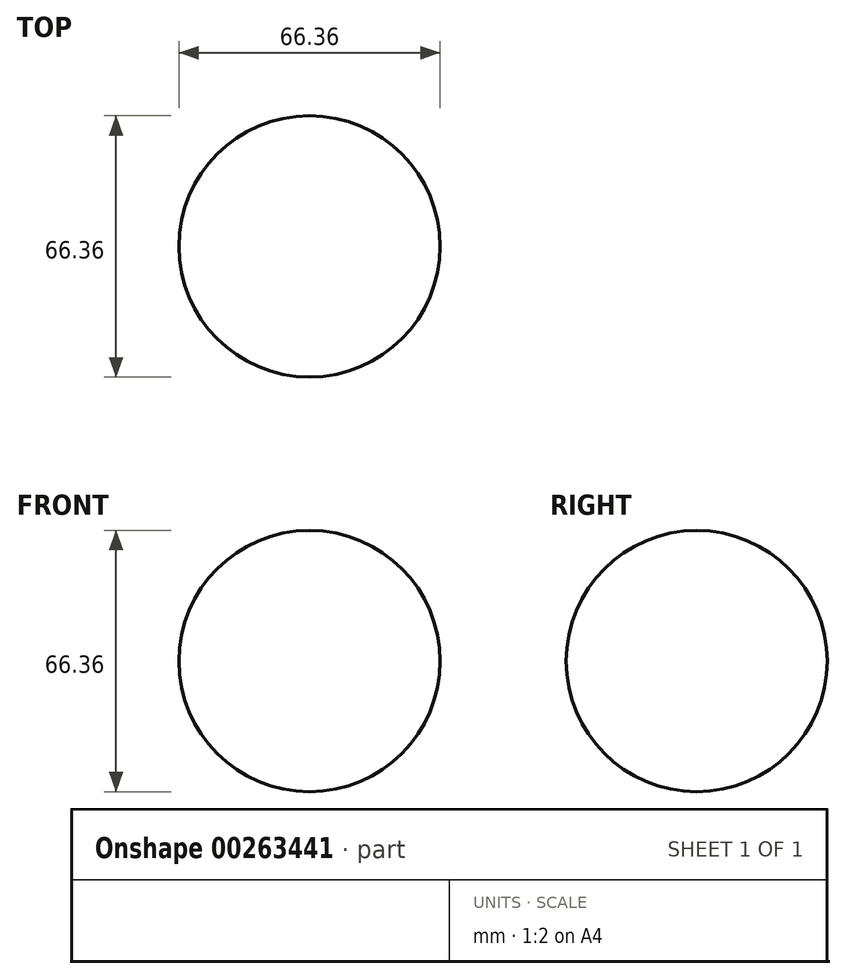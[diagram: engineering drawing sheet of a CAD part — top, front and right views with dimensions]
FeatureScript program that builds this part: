
annotation { "Feature Type Name" : "Feature", "Feature Type Description" : "" }
export const myFeature = defineFeature(function(context is Context, id is Id, definition is map)
    precondition{}
    {
        {
            var Q0;
            Q0=qCreatedBy(makeId("Front.planeOp"),FACE);
            var sketch = newSketch(context, id + "F0", { "sketchPlane" : qUnion([Q0])});
            skArc(sketch, "E0", {"start": v(0, 33.18) * mm, "mid": v(-33.18, 0) * mm, "end": v(0, -33.18) * mm});
            skSolve(sketch);
        }
        {
            var Q0;
            Q0=qCreatedBy(makeId("Front.planeOp"),FACE);
            var sketch = newSketch(context, id + "F1", { "sketchPlane" : qUnion([Q0])});
            skLineSegment(sketch, "E1", {"start": v(0, 44.71) * mm, "end": v(0, -44.48) * mm, "construction": true});
            skSolve(sketch);
        }
        {
            var Q0;
            Q0=sQuery(id+"F0.wireOp",EDGE,"E0");
            var Q1;
            Q1=sQuery(id+"F1.wireOp",EDGE,"E1");
            revolve(context, id + "F2", {"bodyType" : ToolBodyType.SURFACE, "surfaceEntities" : qUnion([Q0]), "axis" : qUnion([Q1]), "revolveType" : RevolveType.FULL});
        }
    });
